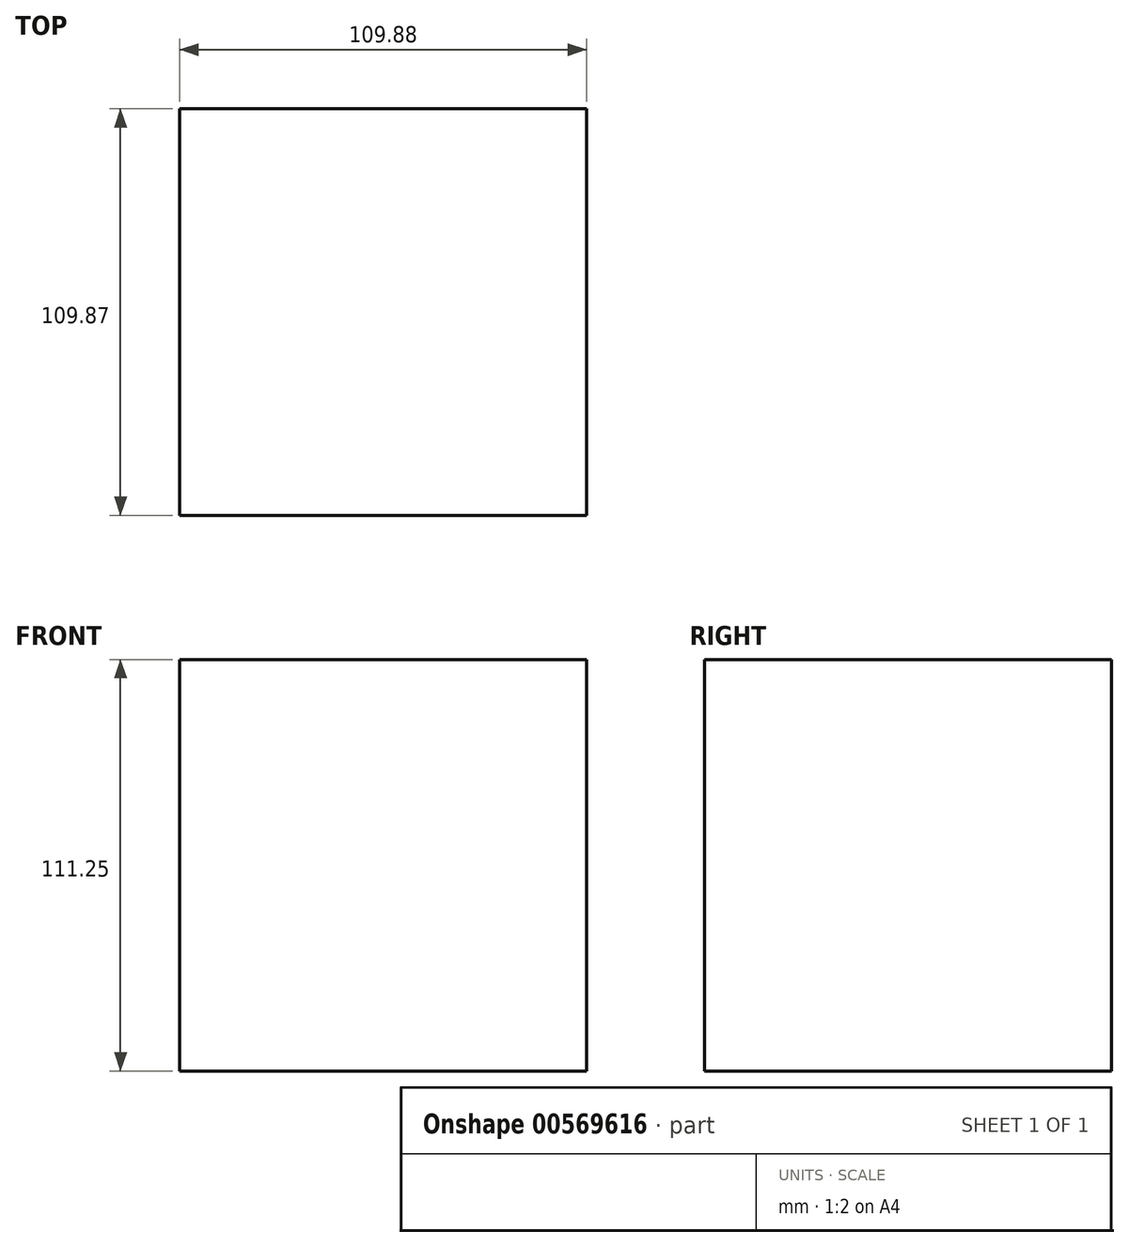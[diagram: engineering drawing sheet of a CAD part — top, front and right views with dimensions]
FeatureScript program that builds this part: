
annotation { "Feature Type Name" : "Feature", "Feature Type Description" : "" }
export const myFeature = defineFeature(function(context is Context, id is Id, definition is map)
    precondition{}
    {
        {
            var Q0;
            Q0=qCreatedBy(makeId("Top.planeOp"),FACE);
            var sketch = newSketch(context, id + "F0", { "sketchPlane" : qUnion([Q0])});
            skLineSegment(sketch, "E0.bottom", {"start": v(-57.15, 60.65) * mm, "end": v(52.73, 60.65) * mm});
            skLineSegment(sketch, "E0.top", {"start": v(-57.15, -49.22) * mm, "end": v(52.73, -49.22) * mm});
            skLineSegment(sketch, "E0.left", {"start": v(-57.15, 60.65) * mm, "end": v(-57.15, -49.22) * mm});
            skLineSegment(sketch, "E0.right", {"start": v(52.73, 60.65) * mm, "end": v(52.73, -49.22) * mm});
            skSolve(sketch);
        }
        {
            var Q0;
            Q0 = qSketchRegion(id + "F0", true);
            extrude(context, id + "F1", {"entities" : qUnion([Q0]), "depth" : 111.25 * mm, "offsetDistance" : 25.4 * mm});
        }
    });
